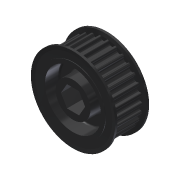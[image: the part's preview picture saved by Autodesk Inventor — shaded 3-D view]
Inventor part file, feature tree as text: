
AUTODESK INVENTOR PART (.ipt)
format: ipt  version: 2013 (Build 170138000, 138)  size: 972,288 bytes
history: native  units: in
note: dims shown in document units (in); Inventor stores cm internally (conversion verified against a paired STEP export)
features: mirror x1, other x1, imported_body x1
ambient origin geometry x8: Origin, YZ Plane, XZ Plane, XY Plane, X Axis, Y Axis, Z Axis, Center Point
feature tree (3):
  mirror  "Mirror1"
  other  "217-3230-STEP1"
  imported_body  "Base1"
